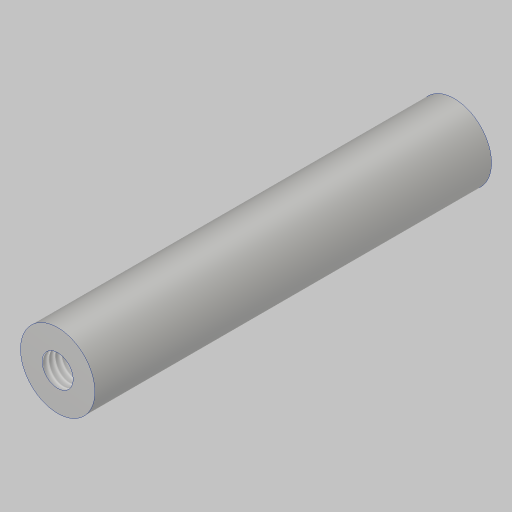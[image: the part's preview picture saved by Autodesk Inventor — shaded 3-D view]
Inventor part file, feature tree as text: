
AUTODESK INVENTOR PART (.ipt)
format: ipt  version: 2023.5 (Build 275446000, 446)  size: 109,568 bytes
history: native  units: in
note: dims shown in document units (in); Inventor stores cm internally (conversion verified against a paired STEP export)
features: extrude x1, hole x1
ambient origin geometry x8: Origin, YZ Plane, XZ Plane, XY Plane, X Axis, Y Axis, Z Axis, Center Point
bodies: Solid1 (feature_tree)
feature tree (2):
  extrude  "Extrusion1"  Depth=2.0in
  hole  "Hole1"  [1 undecoded]
note: 1 required parameter value undecoded (feature->parameter linkage not recoverable at this tier; creation-order binding heuristic only, values carry confidence <= 0.55)
